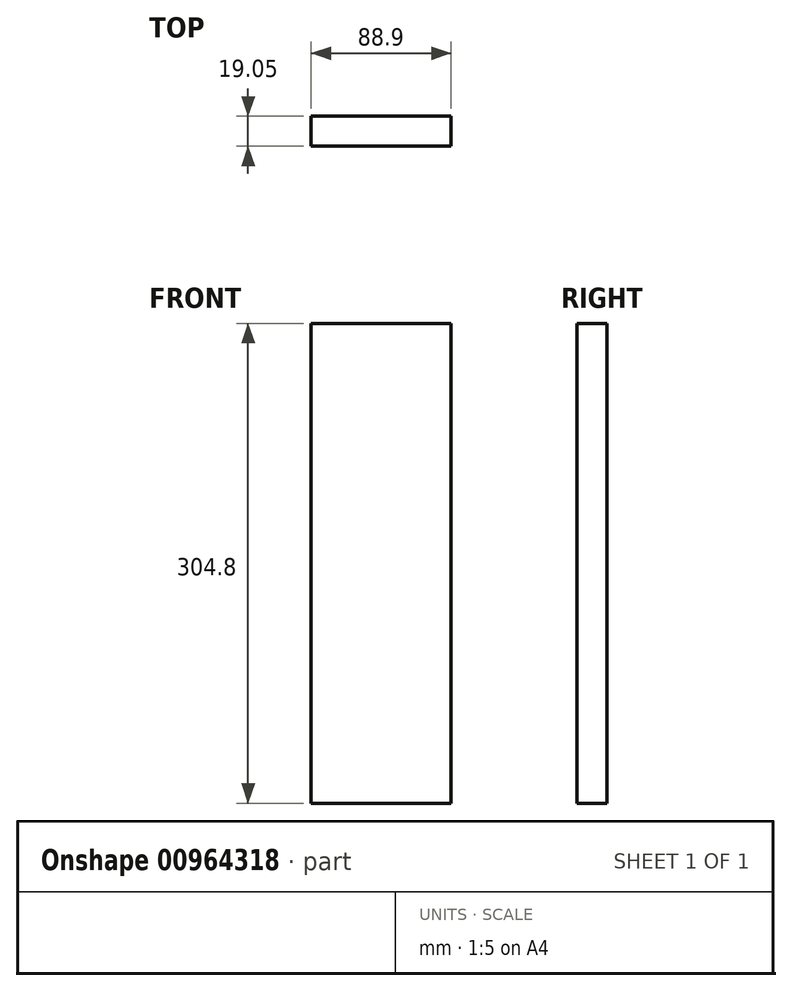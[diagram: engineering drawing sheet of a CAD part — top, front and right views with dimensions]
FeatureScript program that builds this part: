
annotation { "Feature Type Name" : "Feature", "Feature Type Description" : "" }
export const myFeature = defineFeature(function(context is Context, id is Id, definition is map)
    precondition{}
    {
        {
            var Q0;
            Q0=qCreatedBy(makeId("Front.planeOp"),FACE);
            var sketch = newSketch(context, id + "F0", { "sketchPlane" : qUnion([Q0])});
            skLineSegment(sketch, "E0.bottom", {"start": v(-44.45, 152.4) * mm, "end": v(44.45, 152.4) * mm});
            skLineSegment(sketch, "E0.top", {"start": v(-44.45, -152.4) * mm, "end": v(44.45, -152.4) * mm});
            skLineSegment(sketch, "E0.left", {"start": v(-44.45, 152.4) * mm, "end": v(-44.45, -152.4) * mm});
            skLineSegment(sketch, "E0.right", {"start": v(44.45, 152.4) * mm, "end": v(44.45, -152.4) * mm});
            skPoint(sketch, "E0.middle", {"position": v(0, 0) * mm});
            skSolve(sketch);
        }
        {
            var Q0;
            Q0=qSketchRegion(id+"F0",true);
            extrude(context, id + "F1", {"entities" : qUnion([Q0]), "depth" : 19.05 * mm, "offsetDistance" : 25.4 * mm});
        }
    });
